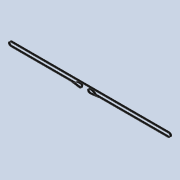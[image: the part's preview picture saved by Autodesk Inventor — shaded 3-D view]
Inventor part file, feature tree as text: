
AUTODESK INVENTOR PART (.ipt)
format: ipt  version: 2020 (Build 240168000, 168)  size: 209,408 bytes
history: native  units: mm
features: reference x7, sketch x6, other x4, extrude x2, sweep x2, projected_geometry x2
ambient origin geometry x8: Origin, YZ Plane, XZ Plane, XY Plane, X Axis, Y Axis, Z Axis, Center Point
bodies: Solid1 (feature_tree), Solid4 (feature_tree), Solid5 (feature_tree)
feature tree (23):
  extrude  "Extrusion1"  Depth=12.0mm
  extrude  "Extrusion3"  Depth=6.0mm TaperAngle=0.0deg
  sweep  "Sweep3"
  sweep  "Sweep4"
  sketch  "Sketch1"  dims[d0=526.0mm d1=12.0mm]
  sketch  "Sketch7"  dims[d2=1.0mm d3=6.0mm d4=0.0mm]
  reference  "Reference3"
  reference  "Reference4"
  sketch  "Sketch8"  dims[d11=10.0mm d13=10.0mm d14=0.0mm]
  reference  "Reference5"
  reference  "Reference6"
  sketch  "Sketch9"  dims[d15=0.0mm d16=0.0mm d17=10.0mm]
  projected_geometry  "Projected Loop3"
  reference  "Reference7"
  sketch  "Sketch10"  dims[d18=0.0mm d19=0.0mm]
  reference  "Reference8"
  reference  "Reference9"
  sketch  "Sketch11"
  projected_geometry  "Projected Loop4"
  parser-record x1  (decoder bookkeeping rows leaked as tree rows — omitted from the tree; the rows remain in map.json)
  other  "0005-10-03 Y axis.iam"
  other  "0005-10-014 Suport Bed.ipt:2"
  other  "0005-10-013 Bed.ipt:7"
note: 1 file-system path scrubbed to <path> (originals preserved in map.json)
